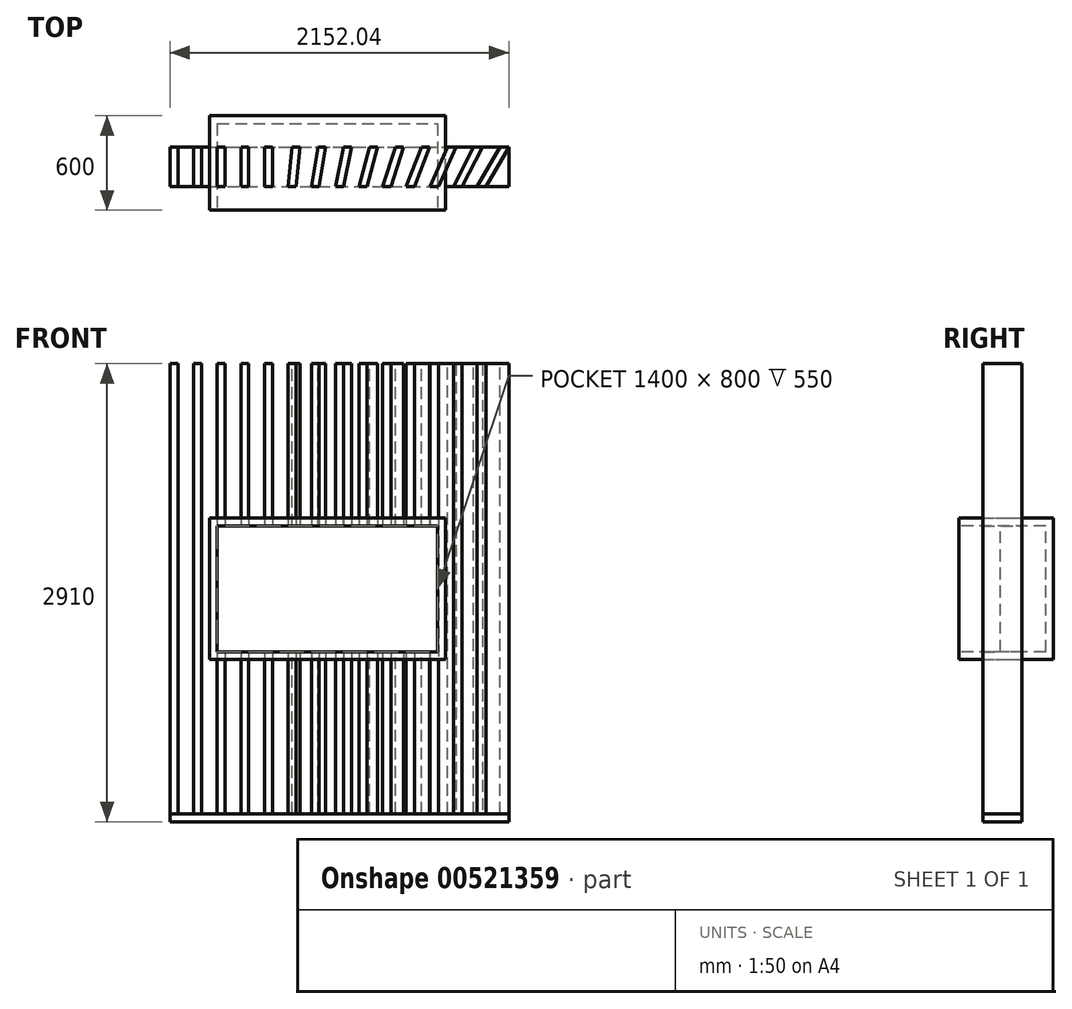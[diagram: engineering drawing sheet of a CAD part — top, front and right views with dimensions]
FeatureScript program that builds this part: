
annotation { "Feature Type Name" : "Feature", "Feature Type Description" : "" }
export const myFeature = defineFeature(function(context is Context, id is Id, definition is map)
    precondition{}
    {
        {
            var Q0;
            Q0=qCreatedBy(makeId("Top.planeOp"),FACE);
            var sketch = newSketch(context, id + "F0", { "sketchPlane" : qUnion([Q0])});
            skLineSegment(sketch, "E0.bottom", {"start": v(0, 0) * mm, "end": v(50, 0) * mm});
            skLineSegment(sketch, "E0.top", {"start": v(0, 250) * mm, "end": v(50, 250) * mm});
            skLineSegment(sketch, "E0.left", {"start": v(0, 0) * mm, "end": v(0, 250) * mm});
            skLineSegment(sketch, "E0.right", {"start": v(50, 0) * mm, "end": v(50, 250) * mm});
            skLineSegment(sketch, "E1.bottom", {"start": v(150, 0) * mm, "end": v(200, 0) * mm});
            skLineSegment(sketch, "E1.top", {"start": v(150, 250) * mm, "end": v(200, 250) * mm});
            skLineSegment(sketch, "E1.left", {"start": v(150, 0) * mm, "end": v(150, 250) * mm});
            skLineSegment(sketch, "E1.right", {"start": v(200, 0) * mm, "end": v(200, 250) * mm});
            skLineSegment(sketch, "E2.bottom", {"start": v(300, 0) * mm, "end": v(350, 0) * mm});
            skLineSegment(sketch, "E2.top", {"start": v(300, 250) * mm, "end": v(350, 250) * mm});
            skLineSegment(sketch, "E2.left", {"start": v(300, 0) * mm, "end": v(300, 250) * mm});
            skLineSegment(sketch, "E2.right", {"start": v(350, 0) * mm, "end": v(350, 250) * mm});
            skLineSegment(sketch, "E3.bottom", {"start": v(450, 0) * mm, "end": v(500, 0) * mm});
            skLineSegment(sketch, "E3.top", {"start": v(450, 250) * mm, "end": v(500, 250) * mm});
            skLineSegment(sketch, "E3.left", {"start": v(450, 0) * mm, "end": v(450, 250) * mm});
            skLineSegment(sketch, "E3.right", {"start": v(500, 0) * mm, "end": v(500, 250) * mm});
            skLineSegment(sketch, "E4.bottom", {"start": v(600, 0) * mm, "end": v(650, 0) * mm});
            skLineSegment(sketch, "E4.top", {"start": v(600, 250) * mm, "end": v(650, 250) * mm});
            skLineSegment(sketch, "E4.left", {"start": v(600, 0) * mm, "end": v(600, 250) * mm});
            skLineSegment(sketch, "E4.right", {"start": v(650, 0) * mm, "end": v(650, 250) * mm});
            skLineSegment(sketch, "E5", {"start": v(750, 0) * mm, "end": v(799.73, -5.23) * mm});
            skLineSegment(sketch, "E6", {"start": v(799.73, -5.23) * mm, "end": v(826.55, 250) * mm});
            skLineSegment(sketch, "E7", {"start": v(826.55, 250) * mm, "end": v(776.59, 255.25) * mm});
            skLineSegment(sketch, "E8", {"start": v(776.59, 255.25) * mm, "end": v(750, 0) * mm});
            skLineSegment(sketch, "E9", {"start": v(1932.23, 259.5) * mm, "end": v(1800, 0) * mm});
            skLineSegment(sketch, "E10", {"start": v(1800, 0) * mm, "end": v(1844.55, -22.7) * mm});
            skLineSegment(sketch, "E11", {"start": v(1844.55, -22.7) * mm, "end": v(1985.8, 254.52) * mm});
            skLineSegment(sketch, "E12", {"start": v(1985.8, 254.52) * mm, "end": v(1932.23, 259.5) * mm});
            skLineSegment(sketch, "E13", {"start": v(2179.98, 392.6) * mm, "end": v(1950, 0) * mm});
            skLineSegment(sketch, "E14", {"start": v(1950, 0) * mm, "end": v(1994.14, -23.5) * mm});
            skLineSegment(sketch, "E15", {"start": v(1994.14, -23.5) * mm, "end": v(2220.77, 369.05) * mm});
            skLineSegment(sketch, "E16", {"start": v(2220.77, 369.05) * mm, "end": v(2179.98, 392.6) * mm});
            skLineSegment(sketch, "E17", {"start": v(900, 0) * mm, "end": v(944.22, -23.34) * mm});
            skLineSegment(sketch, "E18", {"start": v(944.22, -23.34) * mm, "end": v(1000.9, 334.57) * mm});
            skLineSegment(sketch, "E19", {"start": v(1000.9, 334.57) * mm, "end": v(954.16, 341.97) * mm});
            skLineSegment(sketch, "E20", {"start": v(954.16, 341.97) * mm, "end": v(900, 0) * mm});
            skLineSegment(sketch, "E21", {"start": v(1050, 0) * mm, "end": v(1098.9, -10.4) * mm});
            skLineSegment(sketch, "E22", {"start": v(1098.9, -10.4) * mm, "end": v(1171.25, 329.97) * mm});
            skLineSegment(sketch, "E23", {"start": v(1171.25, 329.97) * mm, "end": v(1122.35, 340.37) * mm});
            skLineSegment(sketch, "E24", {"start": v(1122.35, 340.37) * mm, "end": v(1050, 0) * mm});
            skLineSegment(sketch, "E25", {"start": v(1200, 0) * mm, "end": v(1247.59, -15.34) * mm});
            skLineSegment(sketch, "E26", {"start": v(1247.59, -15.34) * mm, "end": v(1336.02, 314.68) * mm});
            skLineSegment(sketch, "E27", {"start": v(1336.02, 314.68) * mm, "end": v(1287.78, 327.6) * mm});
            skLineSegment(sketch, "E28", {"start": v(1287.78, 327.6) * mm, "end": v(1200, 0) * mm});
            skLineSegment(sketch, "E29", {"start": v(0, 0) * mm, "end": v(3271.2, 0) * mm, "construction": true});
            skLineSegment(sketch, "E30", {"start": v(1350, 0) * mm, "end": v(1397.55, -15.45) * mm});
            skLineSegment(sketch, "E31", {"start": v(1397.55, -15.45) * mm, "end": v(1483.8, 250) * mm});
            skLineSegment(sketch, "E32", {"start": v(1483.8, 250) * mm, "end": v(1483.8, 250) * mm});
            skLineSegment(sketch, "E33", {"start": v(1436.44, 266.03) * mm, "end": v(1350, 0) * mm});
            skLineSegment(sketch, "E34", {"start": v(1500, 0) * mm, "end": v(1546.68, -17.92) * mm});
            skLineSegment(sketch, "E35", {"start": v(1546.68, -17.92) * mm, "end": v(1650.89, 253.55) * mm});
            skLineSegment(sketch, "E36", {"start": v(1650.89, 253.55) * mm, "end": v(1601.42, 264.2) * mm});
            skLineSegment(sketch, "E37", {"start": v(1601.42, 264.2) * mm, "end": v(1500, 0) * mm});
            skLineSegment(sketch, "E38", {"start": v(1650, 0) * mm, "end": v(1697.16, -16.61) * mm});
            skLineSegment(sketch, "E39", {"start": v(1697.16, -16.61) * mm, "end": v(1821.15, 261.87) * mm});
            skLineSegment(sketch, "E40", {"start": v(1821.15, 261.87) * mm, "end": v(1775.62, 282.14) * mm});
            skLineSegment(sketch, "E41", {"start": v(1775.62, 282.14) * mm, "end": v(1650, 0) * mm});
            skLineSegment(sketch, "E42", {"start": v(0, 250) * mm, "end": v(2297.86, 250) * mm, "construction": true});
            skLineSegment(sketch, "E43", {"start": v(1483.8, 250) * mm, "end": v(1436.44, 266.03) * mm});
            skSolve(sketch);
        }
        {
            var Q0;
            Q0 = qSketchRegion(id + "F0", true);
            extrude(context, id + "F1", {"entities" : qUnion([Q0]), "depth" : 2860 * mm, "offsetDistance" : 25 * mm});
        }
        {
            var Q0;
            Q0=qCreatedBy(makeId("Top.planeOp"),FACE);
            var sketch = newSketch(context, id + "F2", { "sketchPlane" : qUnion([Q0])});
            skLineSegment(sketch, "E44.bottom", {"start": v(0, 0) * mm, "end": v(2221.7, 0) * mm});
            skLineSegment(sketch, "E44.top", {"start": v(0, 250) * mm, "end": v(2221.7, 250) * mm});
            skLineSegment(sketch, "E44.left", {"start": v(0, 0) * mm, "end": v(0, 250) * mm});
            skLineSegment(sketch, "E44.right", {"start": v(2221.7, 0) * mm, "end": v(2221.7, 250) * mm});
            skSolve(sketch);
        }
        {
            var Q0;
            Q0 = qSketchRegion(id + "F2", true);
            extrude(context, id + "F3", {"entities" : qUnion([Q0]), "operationType" : NewBodyOperationType.INTERSECT, "endBound" : BoundingType.THROUGH_ALL, "depth" : 25 * mm, "offsetDistance" : 25 * mm});
        }
        {
            var Q0;
            Q0=makeQuery(id+"F1.opExtrude","CAP_FACE",FACE,{"disambiguationData":[OSD([sQuery(id+"F0.wireOp",EDGE,"E0.bottom"),sQuery(id+"F0.wireOp",EDGE,"E0.top"),sQuery(id+"F0.wireOp",EDGE,"E0.left"),sQuery(id+"F0.wireOp",EDGE,"E0.right")])],"isStart":false});
            var Q1;
            Q1=makeQuery(id+"F1.opExtrude","CAP_FACE",FACE,{"disambiguationData":[OSD([sQuery(id+"F0.wireOp",EDGE,"E0.bottom"),sQuery(id+"F0.wireOp",EDGE,"E0.top"),sQuery(id+"F0.wireOp",EDGE,"E0.left"),sQuery(id+"F0.wireOp",EDGE,"E0.right")])],"isStart":true});
            cPlane(context, id + "F4", {"entities" : qUnion([Q0, Q1]), "cplaneType" : CPlaneType.MID_PLANE, "offset" : 25 * mm, "width" : 150 * mm, "height" : 150 * mm});
        }
        {
            var Q0;
            Q0=qCreatedBy(makeId("Top.planeOp"),FACE);
            var sketch = newSketch(context, id + "F5", { "sketchPlane" : qUnion([Q0])});
            skLineSegment(sketch, "E45.bottom", {"start": v(0, 250) * mm, "end": v(2152.04, 250) * mm});
            skLineSegment(sketch, "E45.top", {"start": v(0, 0) * mm, "end": v(2152.04, 0) * mm});
            skLineSegment(sketch, "E45.left", {"start": v(0, 250) * mm, "end": v(0, 0) * mm});
            skLineSegment(sketch, "E45.right", {"start": v(2152.04, 250) * mm, "end": v(2152.04, 0) * mm});
            skSolve(sketch);
        }
        {
            var Q0;
            Q0 = qSketchRegion(id + "F5", true);
            extrude(context, id + "F6", {"entities" : qUnion([Q0]), "oppositeDirection" : true, "depth" : 50 * mm, "offsetDistance" : 25 * mm});
        }
        {
            var Q0;
            Q0=qCreatedBy(makeId("Front.planeOp"),FACE);
            var sketch = newSketch(context, id + "F7", { "sketchPlane" : qUnion([Q0])});
            skLineSegment(sketch, "E46.bottom", {"start": v(250, 980) * mm, "end": v(1750, 980) * mm});
            skLineSegment(sketch, "E46.top", {"start": v(250, 1880) * mm, "end": v(1750, 1880) * mm});
            skLineSegment(sketch, "E46.left", {"start": v(250, 980) * mm, "end": v(250, 1880) * mm});
            skLineSegment(sketch, "E46.right", {"start": v(1750, 980) * mm, "end": v(1750, 1880) * mm});
            skSolve(sketch);
        }
        {
            var Q0;
            Q0=makeQuery(id+"F7.imprint","IMPRINT",FACE,{"disambiguationData":[TD([[makeQuery(id+"F7.imprint","IMPRINT",EDGE,{"derivedFrom":sQuery(id+"F7.wireOp",EDGE,"E46.bottom")}),1.0]])]});
            extrude(context, id + "F8", {"entities" : qUnion([Q0]), "depth" : 150 * mm, "offsetDistance" : 25 * mm, "hasSecondDirection" : true, "secondDirectionOppositeDirection" : true, "secondDirectionDepth" : 450 * mm});
        }
        {
            var Q0;
            Q0=makeQuery(id+"F8.opExtrude","SWEPT_BODY",BODY,{"disambiguationData":[OSD([sQuery(id+"F7.wireOp",EDGE,"E46.bottom"),sQuery(id+"F7.wireOp",EDGE,"E46.top"),sQuery(id+"F7.wireOp",EDGE,"E46.left"),sQuery(id+"F7.wireOp",EDGE,"E46.right")])]});
            var Q1;
            Q1=makeQuery(id+"F6.opExtrude","SWEPT_BODY",BODY,{"disambiguationData":[OSD([sQuery(id+"F5.wireOp",EDGE,"E45.bottom"),sQuery(id+"F5.wireOp",EDGE,"E45.top"),sQuery(id+"F5.wireOp",EDGE,"E45.left"),sQuery(id+"F5.wireOp",EDGE,"E45.right")])]});
            booleanBodies(context, id + "F9", {"operationType" : BooleanOperationType.SUBTRACTION, "tools" : qUnion([Q0]), "targets" : qUnion([Q1]), "keepTools" : true});
        }
        {
            var Q0;
            Q0=makeQuery(id+"F8.opExtrude","CAP_FACE",FACE,{"disambiguationData":[OSD([sQuery(id+"F7.wireOp",EDGE,"E46.bottom"),sQuery(id+"F7.wireOp",EDGE,"E46.top"),sQuery(id+"F7.wireOp",EDGE,"E46.left"),sQuery(id+"F7.wireOp",EDGE,"E46.right")])],"isStart":false});
            var sketch = newSketch(context, id + "F10", { "sketchPlane" : qUnion([Q0])});
            skLineSegment(sketch, "E47.bottom", {"start": v(300, 1030) * mm, "end": v(1700, 1030) * mm});
            skLineSegment(sketch, "E47.top", {"start": v(300, 1830) * mm, "end": v(1700, 1830) * mm});
            skLineSegment(sketch, "E47.left", {"start": v(300, 1030) * mm, "end": v(300, 1830) * mm});
            skLineSegment(sketch, "E47.right", {"start": v(1700, 1030) * mm, "end": v(1700, 1830) * mm});
            skSolve(sketch);
        }
        {
            var Q0;
            Q0 = qSketchRegion(id + "F10", true);
            extrude(context, id + "F11", {"entities" : qUnion([Q0]), "operationType" : NewBodyOperationType.REMOVE, "oppositeDirection" : true, "depth" : 550 * mm, "offsetDistance" : 25 * mm});
        }
    });
